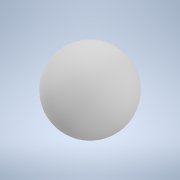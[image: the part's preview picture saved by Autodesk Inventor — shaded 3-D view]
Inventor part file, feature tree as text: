
AUTODESK INVENTOR PART (.ipt)
format: ipt  version: 2020 (Build 240168000, 168)  size: 116,736 bytes
history: native  units: in
note: dims shown in document units (in); Inventor stores cm internally (conversion verified against a paired STEP export)
features: revolve x1, sketch x1
ambient origin geometry x8: Origin, YZ Plane, XZ Plane, XY Plane, X Axis, Y Axis, Z Axis, Center Point
bodies: Solid1 (feature_tree)
feature tree (2):
  revolve  "Revolution1"  Angle=180.0deg
  sketch  "Sketch1"  dims[d0=0.125in d1=180.0deg]
